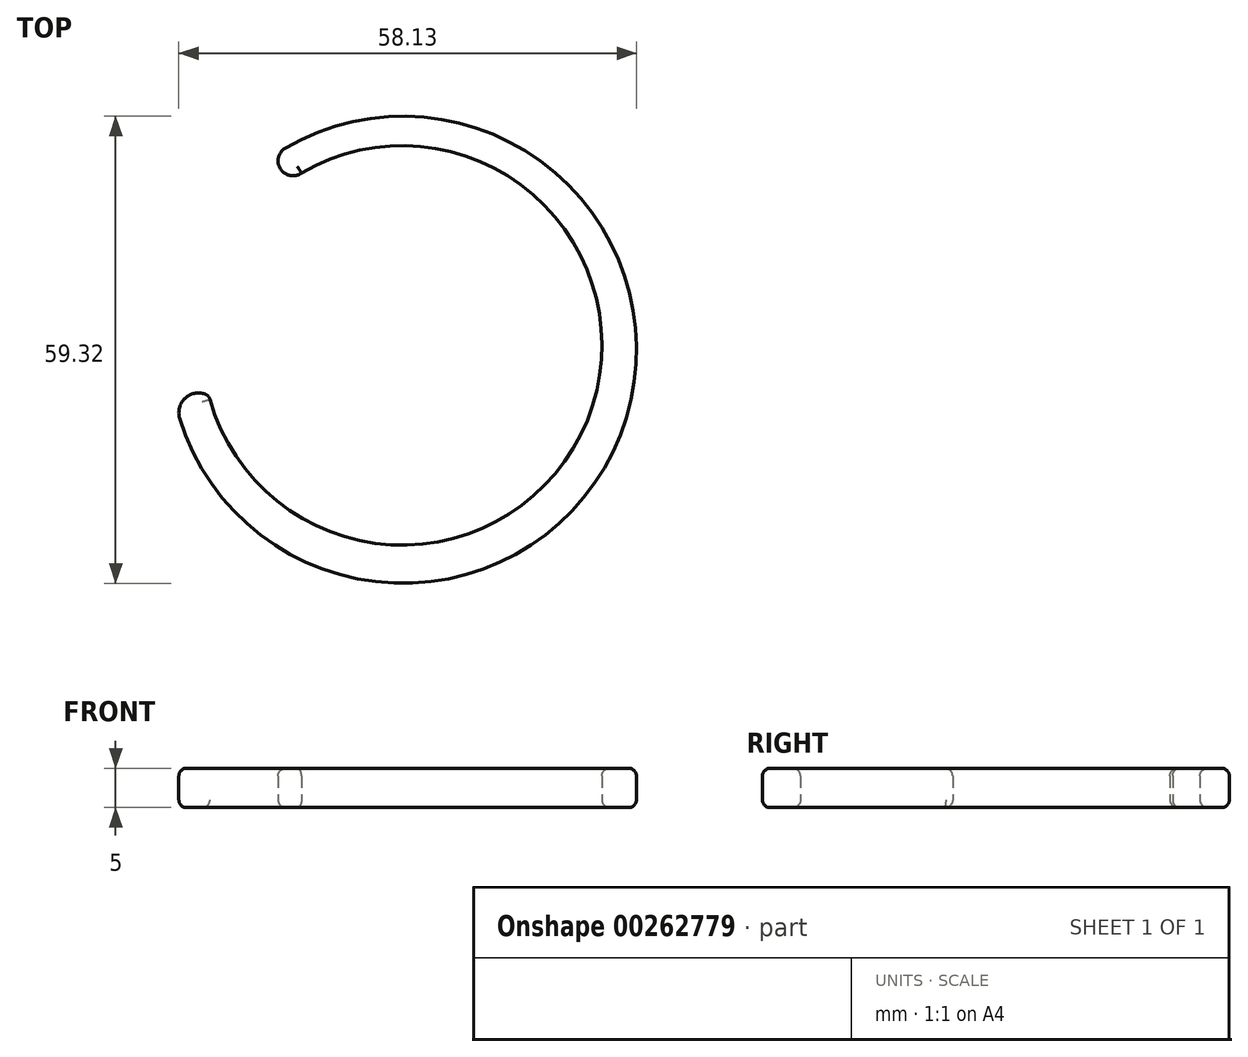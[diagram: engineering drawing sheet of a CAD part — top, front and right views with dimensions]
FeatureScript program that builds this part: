
annotation { "Feature Type Name" : "Feature", "Feature Type Description" : "" }
export const myFeature = defineFeature(function(context is Context, id is Id, definition is map)
    precondition{}
    {
        {
            var Q0;
            Q0=qCreatedBy(makeId("Top.planeOp"),FACE);
            var sketch = newSketch(context, id + "F0", { "sketchPlane" : qUnion([Q0])});
            skArc(sketch, "E0", {"start": v(0, 0) * mm, "mid": v(47.96, -3.27) * mm, "end": v(11.75, 28.35) * mm});
            skArc(sketch, "E1", {"start": v(-3.73, -2.8) * mm, "mid": v(52.25, -4.92) * mm, "end": v(9.7, 31.52) * mm});
            skArc(sketch, "E2", {"start": v(9.7, 31.52) * mm, "mid": v(9.06, 28.86) * mm, "end": v(11.75, 28.35) * mm});
            skArc(sketch, "E3", {"start": v(-3.73, -2.8) * mm, "mid": v(-2.85, -0.09) * mm, "end": v(0, 0) * mm});
            skSolve(sketch);
        }
        {
            var Q0;
            Q0=makeQuery(id+"F0.imprint","IMPRINT",FACE,{"disambiguationData":[TD([[makeQuery(id+"F0.imprint","IMPRINT",EDGE,{"derivedFrom":sQuery(id+"F0.wireOp",EDGE,"E0")}),-1.0]])]});
            extrude(context, id + "F1", {"entities" : qUnion([Q0]), "depth" : 5 * mm});
        }
        {
            var Q0;
            Q0=makeQuery(id+"F1.opExtrude","CAP_EDGE",EDGE,{"disambiguationData":[OSD([sQuery(id+"F0.wireOp",EDGE,"E0")])],"isStart":true});
            fillet(context, id + "F2", {"entities" : qUnion([Q0]), "radius" : 1 * mm, "tangentPropagation" : true, "allowEdgeOverflow" : false});
        }
        {
            var Q0;
            Q0=makeQuery(id+"F1.opExtrude","CAP_EDGE",EDGE,{"disambiguationData":[OSD([sQuery(id+"F0.wireOp",EDGE,"E0")])],"isStart":false});
            var Q1;
            Q1=makeQuery(id+"F1.opExtrude","CAP_EDGE",EDGE,{"disambiguationData":[OSD([sQuery(id+"F0.wireOp",EDGE,"E2")])],"isStart":false});
            fillet(context, id + "F3", {"entities" : qUnion([Q0, Q1]), "radius" : 1 * mm, "tangentPropagation" : true, "allowEdgeOverflow" : false});
        }
        {
            var Q0;
            {var subQ0=sQuery(id+"F0.wireOp",EDGE,"E3");Q0=makeQuery(id+"F3.opFillet","BLEND_EDGE",EDGE,{"blendedFrom":[makeQuery(id+"F1.opExtrude","CAP_EDGE",EDGE,{"disambiguationData":[OSD([subQ0])],"isStart":false}),makeQuery(id+"F1.opExtrude","CAP_FACE",FACE,{"disambiguationData":[OSD([sQuery(id+"F0.wireOp",EDGE,"E0"),sQuery(id+"F0.wireOp",EDGE,"E1"),sQuery(id+"F0.wireOp",EDGE,"E2"),subQ0])],"isStart":false})],"blendedInto":[makeQuery(id+"F1.opExtrude","CAP_FACE",FACE,{"disambiguationData":[OSD([sQuery(id+"F0.wireOp",EDGE,"E0"),sQuery(id+"F0.wireOp",EDGE,"E1"),sQuery(id+"F0.wireOp",EDGE,"E2"),subQ0])],"isStart":false})]});}
            var Q1;
            Q1=makeQuery(id+"F1.opExtrude","CAP_EDGE",EDGE,{"disambiguationData":[OSD([sQuery(id+"F0.wireOp",EDGE,"E2")])],"isStart":true});
            var Q2;
            Q2=makeQuery(id+"F1.opExtrude","CAP_EDGE",EDGE,{"disambiguationData":[OSD([sQuery(id+"F0.wireOp",EDGE,"E3")])],"isStart":true});
            fillet(context, id + "F4", {"entities" : qUnion([Q0, Q1, Q2]), "radius" : 1 * mm, "tangentPropagation" : true, "allowEdgeOverflow" : false});
        }
    });
